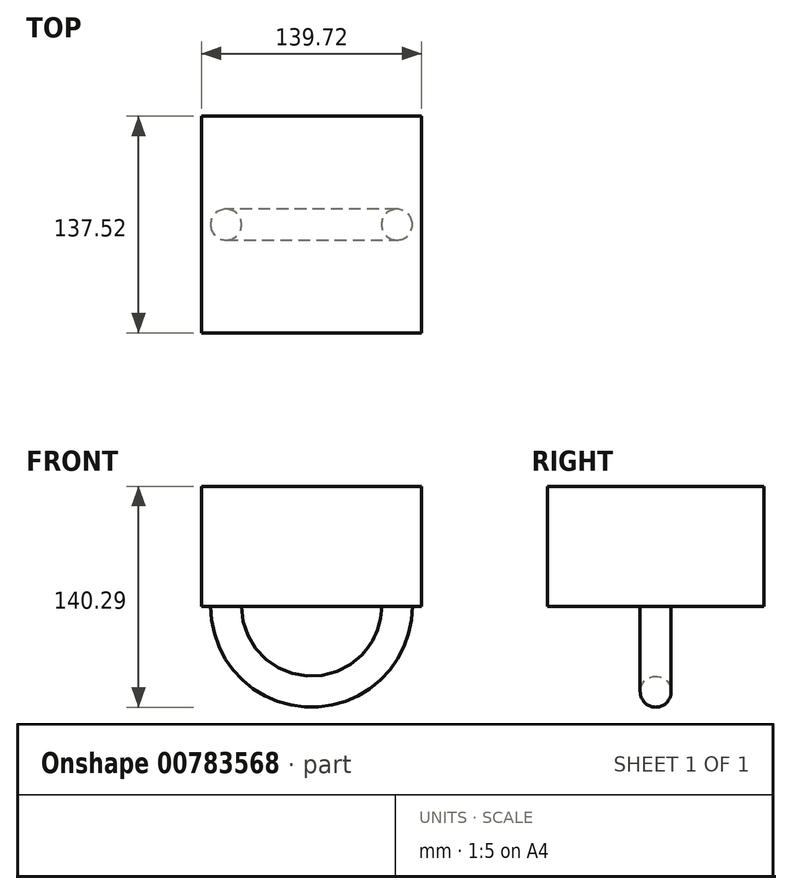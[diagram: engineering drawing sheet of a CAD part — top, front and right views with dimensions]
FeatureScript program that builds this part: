
annotation { "Feature Type Name" : "Feature", "Feature Type Description" : "" }
export const myFeature = defineFeature(function(context is Context, id is Id, definition is map)
    precondition{}
    {
        {
            var Q0;
            Q0=qCreatedBy(makeId("Top.planeOp"),FACE);
            var sketch = newSketch(context, id + "F0", { "sketchPlane" : qUnion([Q0])});
            skLineSegment(sketch, "E0.bottom", {"start": v(69.86, -68.76) * mm, "end": v(-69.86, -68.76) * mm});
            skLineSegment(sketch, "E0.top", {"start": v(69.86, 68.76) * mm, "end": v(-69.86, 68.76) * mm});
            skLineSegment(sketch, "E0.left", {"start": v(69.86, -68.76) * mm, "end": v(69.86, 68.76) * mm});
            skLineSegment(sketch, "E0.right", {"start": v(-69.86, -68.76) * mm, "end": v(-69.86, 68.76) * mm});
            skPoint(sketch, "E0.middle", {"position": v(0, 0) * mm});
            skLineSegment(sketch, "E1", {"start": v(0, 68.76) * mm, "end": v(0, -68.76) * mm});
            skSolve(sketch);
        }
        {
            var Q0;
            Q0=qCreatedBy(makeId("Top.planeOp"),FACE);
            var sketch = newSketch(context, id + "F1", { "sketchPlane" : qUnion([Q0])});
            skCircle(sketch, "E2", {"center": v(54.26, 0) * mm, "radius": 9.82 * mm});
            skSolve(sketch);
        }
        {
            var Q0;
            {var subQ0=sQuery(id+"F0.wireOp",EDGE,"E0.right");Q0=makeQuery(id+"F0.imprint","IMPRINT",FACE,{"disambiguationData":[TD([[makeQuery(id+"F0.imprint","IMPRINT",EDGE,{"derivedFrom":subQ0}),-1.0]])]});}
            var Q1;
            {var subQ0=sQuery(id+"F0.wireOp",EDGE,"E0.left");Q1=makeQuery(id+"F0.imprint","IMPRINT",FACE,{"disambiguationData":[TD([[makeQuery(id+"F0.imprint","IMPRINT",EDGE,{"derivedFrom":subQ0}),1.0]])]});}
            extrude(context, id + "F2", {"entities" : qUnion([Q0, Q1]), "depth" : 50.8 * mm, "offsetDistance" : 25.4 * mm});
        }
        {
            var Q0;
            Q0=makeQuery(id+"F2.opExtrude","CAP_FACE",FACE,{"disambiguationData":[OSD([sQuery(id+"F0.wireOp",EDGE,"E0.bottom"),sQuery(id+"F0.wireOp",EDGE,"E0.top"),sQuery(id+"F0.wireOp",EDGE,"E0.left"),sQuery(id+"F0.wireOp",EDGE,"E0.right")])],"isStart":false});
            extrude(context, id + "F3", {"entities" : qUnion([Q0]), "operationType" : NewBodyOperationType.ADD, "depth" : 25.4 * mm, "offsetDistance" : 25.4 * mm});
        }
        {
            var Q0;
            Q0=makeQuery(id+"F1.imprint","IMPRINT",FACE,{"disambiguationData":[TD([[makeQuery(id+"F1.imprint","IMPRINT",EDGE,{"derivedFrom":sQuery(id+"F1.wireOp",EDGE,"E2")}),1.0]])]});
            var Q1;
            Q1=sQuery(id+"F0.wireOp",EDGE,"E1");
            revolve(context, id + "F4", {"operationType" : NewBodyOperationType.ADD, "surfaceOperationType" : NewSurfaceOperationType.NEW, "entities" : qUnion([Q0]), "axis" : qUnion([Q1]), "revolveType" : RevolveType.ONE_DIRECTION, "oppositeDirection" : true, "angle" : 180 * degree});
        }
    });
